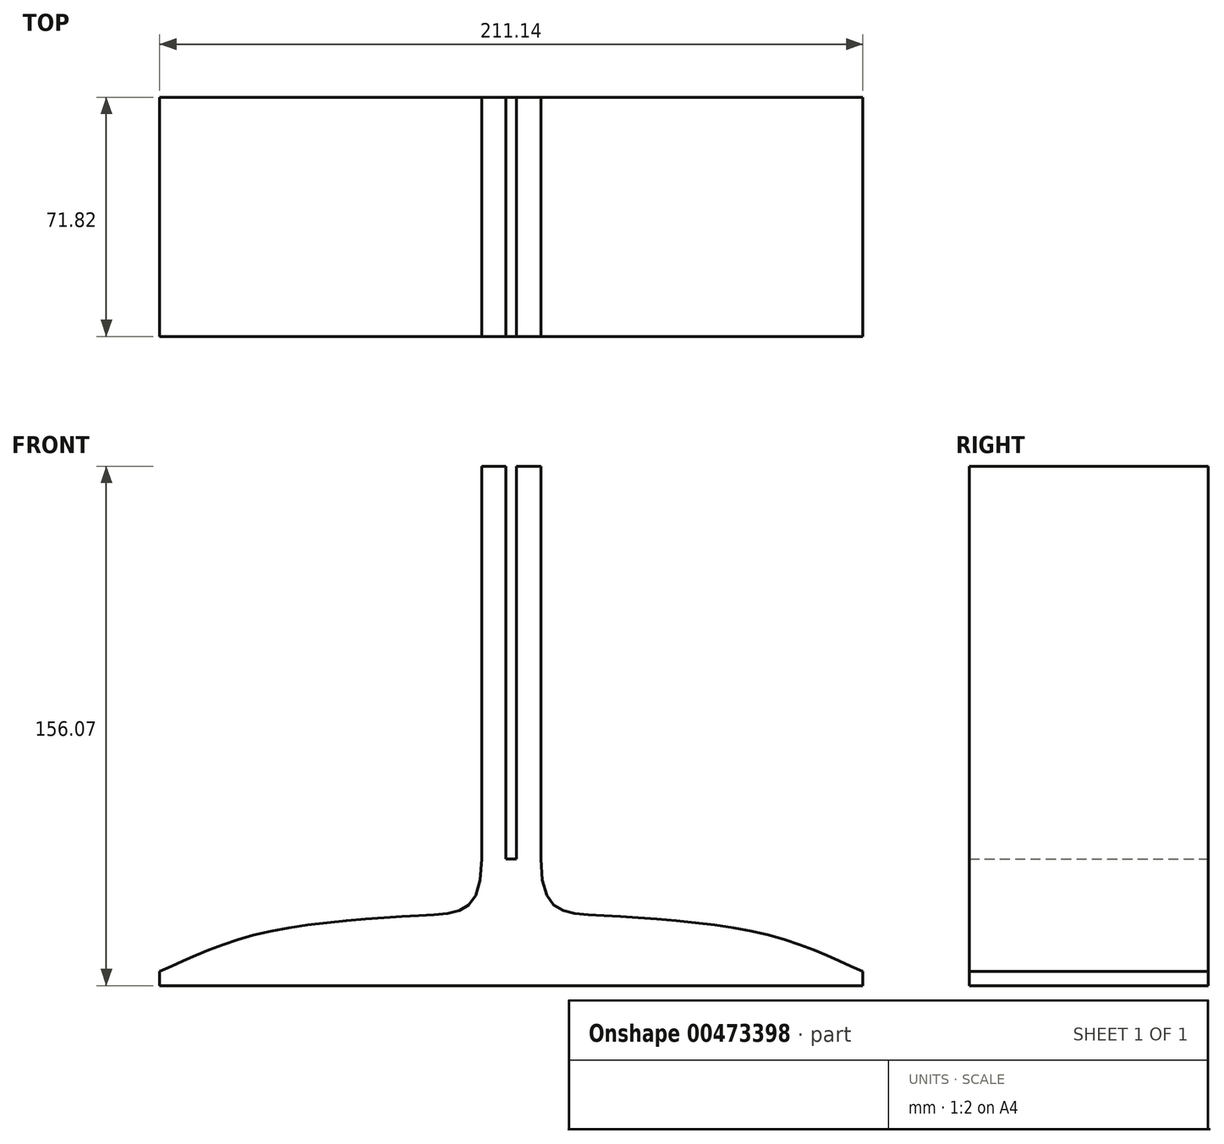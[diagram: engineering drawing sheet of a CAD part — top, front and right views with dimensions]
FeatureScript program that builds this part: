
annotation { "Feature Type Name" : "Feature", "Feature Type Description" : "" }
export const myFeature = defineFeature(function(context is Context, id is Id, definition is map)
    precondition{}
    {
        {
            var Q0;
            Q0=qCreatedBy(makeId("Top.planeOp"),FACE);
            var sketch = newSketch(context, id + "F0", { "sketchPlane" : qUnion([Q0])});
            skLineSegment(sketch, "E0.bottom", {"start": v(105.57, -35.9) * mm, "end": v(-105.57, -35.9) * mm});
            skLineSegment(sketch, "E0.top", {"start": v(105.57, 35.9) * mm, "end": v(-105.57, 35.9) * mm});
            skLineSegment(sketch, "E0.left", {"start": v(105.57, -35.9) * mm, "end": v(105.57, 35.9) * mm});
            skLineSegment(sketch, "E0.right", {"start": v(-105.57, -35.9) * mm, "end": v(-105.57, 35.9) * mm});
            skPoint(sketch, "E0.middle", {"position": v(0, 0) * mm});
            skSolve(sketch);
        }
        {
            var Q0;
            Q0 = qSketchRegion(id + "F0", true);
            extrude(context, id + "F1", {"entities" : qUnion([Q0]), "depth" : 38.1 * mm});
        }
        {
            var Q0;
            Q0=makeQuery(id+"F1.opExtrude","SWEPT_FACE",FACE,{"disambiguationData":[OSD([sQuery(id+"F0.wireOp",EDGE,"E0.bottom")])]});
            var sketch = newSketch(context, id + "F2", { "sketchPlane" : qUnion([Q0])});
            skSolve(sketch);
        }
        {
            var Q0;
            {var subQ0=sQuery(id+"F0.wireOp",EDGE,"E0.bottom");Q0=makeQuery(id+"F2.imprint","IMPRINT",FACE,{"disambiguationData":[TD([[makeQuery(id+"F2.imprint","IMPRINT",EDGE,{"derivedFrom":makeQuery(id+"F1.opExtrude","CAP_EDGE",EDGE,{"disambiguationData":[OSD([subQ0])],"isStart":true})}),-1.0]])]});}
            var sketch = newSketch(context, id + "F3", { "sketchPlane" : qUnion([Q0])});
            skLineSegment(sketch, "E1.bottom", {"start": v(8.9, 19.05) * mm, "end": v(-8.89, 19.05) * mm});
            skLineSegment(sketch, "E1.top", {"start": v(8.89, 156.07) * mm, "end": v(1.59, 156.07) * mm});
            skLineSegment(sketch, "E1.left", {"start": v(8.9, 19.05) * mm, "end": v(8.89, 156.07) * mm});
            skLineSegment(sketch, "E1.right", {"start": v(-8.89, 19.05) * mm, "end": v(-8.9, 156.07) * mm});
            skPoint(sketch, "E1.middle", {"position": v(0, 87.56) * mm});
            skLineSegment(sketch, "E2.bottom", {"start": v(1.59, 25.96) * mm, "end": v(-1.59, 25.96) * mm});
            skLineSegment(sketch, "E2.left", {"start": v(1.59, 25.96) * mm, "end": v(1.59, 156.07) * mm});
            skLineSegment(sketch, "E2.right", {"start": v(-1.59, 25.96) * mm, "end": v(-1.59, 156.07) * mm});
            skPoint(sketch, "E2.middle", {"position": v(0, 72.95) * mm});
            skLineSegment(sketch, "E3.trimOffspring", {"start": v(-1.59, 156.07) * mm, "end": v(-8.9, 156.07) * mm});
            skSolve(sketch);
        }
        {
            var Q0;
            Q0 = qSketchRegion(id + "F3", true);
            var Q1;
            Q1=makeQuery(id+"F1.opExtrude","SWEPT_FACE",FACE,{"disambiguationData":[OSD([sQuery(id+"F0.wireOp",EDGE,"E0.top")])]});
            extrude(context, id + "F4", {"entities" : qUnion([Q0]), "operationType" : NewBodyOperationType.ADD, "endBound" : BoundingType.UP_TO_SURFACE, "oppositeDirection" : true, "endBoundEntityFace" : qUnion([Q1]), "depth" : 25.4 * mm});
        }
        {
            var Q0;
            {var subQ0=sQuery(id+"F0.wireOp",EDGE,"E0.bottom");Q0=makeQuery(id+"F2.imprint","IMPRINT",FACE,{"disambiguationData":[TD([[makeQuery(id+"F2.imprint","IMPRINT",EDGE,{"derivedFrom":makeQuery(id+"F1.opExtrude","CAP_EDGE",EDGE,{"disambiguationData":[OSD([subQ0])],"isStart":true})}),-1.0]])]});}
            var sketch = newSketch(context, id + "F5", { "sketchPlane" : qUnion([Q0])});
            skFitSpline(sketch, "E4", {"points": [v(-107.04, 3.68) * mm, v(-77.1, 15.24) * mm, v(-24.82, 21.2) * mm, v(-8.9, 38.1) * mm], "startDerivative": vector(81.28, 33.57) * mm, "endDerivative": vector(0, 176.98) * mm});
            skLineSegment(sketch, "E5", {"start": v(0, 0) * mm, "end": v(0, 110.89) * mm, "construction": true});
            skFitSpline(sketch, "E6.MirrorCS", {"points": [v(107.04, 3.68) * mm, v(77.1, 15.24) * mm, v(24.82, 21.2) * mm, v(8.9, 38.1) * mm], "startDerivative": vector(-81.28, 33.57) * mm, "endDerivative": vector(0, 176.98) * mm});
            skLineSegment(sketch, "E7", {"start": v(-107.04, 3.68) * mm, "end": v(-107.04, 43.36) * mm});
            skLineSegment(sketch, "E8", {"start": v(-107.04, 43.36) * mm, "end": v(-8.9, 38.1) * mm});
            skLineSegment(sketch, "E9.MirrorCS", {"start": v(107.04, 43.36) * mm, "end": v(8.9, 38.1) * mm});
            skLineSegment(sketch, "E10.MirrorCS", {"start": v(107.04, 3.68) * mm, "end": v(107.04, 43.36) * mm});
            skSolve(sketch);
        }
        {
            var Q0;
            Q0 = qSketchRegion(id + "F5", true);
            extrude(context, id + "F6", {"entities" : qUnion([Q0]), "operationType" : NewBodyOperationType.REMOVE, "oppositeDirection" : true, "depth" : 90.68 * mm});
        }
    });
